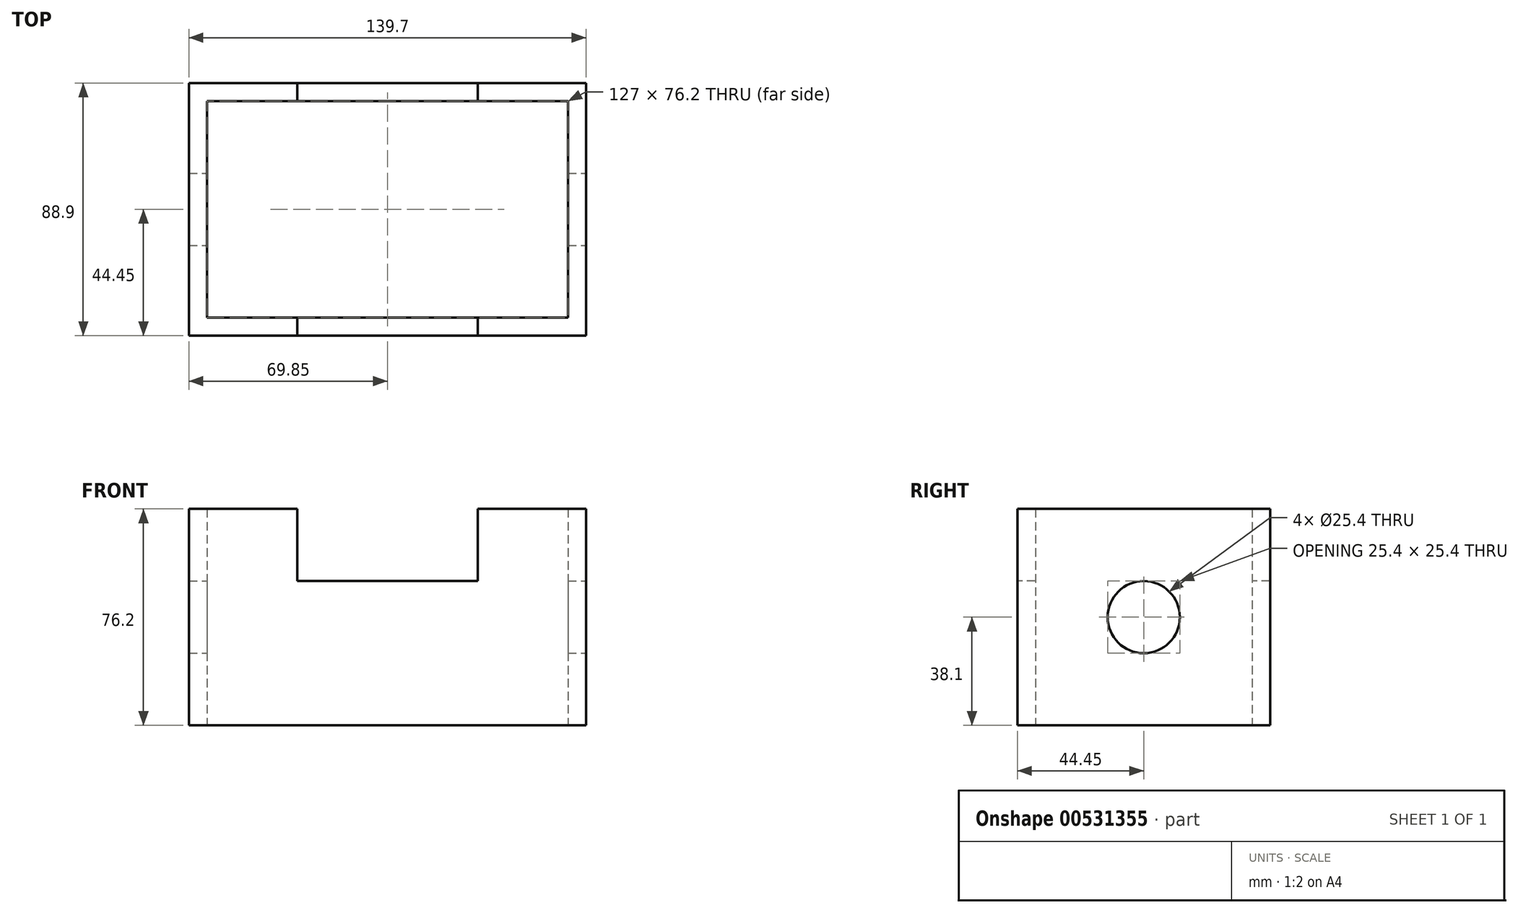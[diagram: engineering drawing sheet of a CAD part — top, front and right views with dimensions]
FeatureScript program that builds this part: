
annotation { "Feature Type Name" : "Feature", "Feature Type Description" : "" }
export const myFeature = defineFeature(function(context is Context, id is Id, definition is map)
    precondition{}
    {
        {
            var Q0;
            Q0=qCreatedBy(makeId("Top.planeOp"),FACE);
            var sketch = newSketch(context, id + "F0", { "sketchPlane" : qUnion([Q0])});
            skLineSegment(sketch, "E0.bottom", {"start": v(63.5, -38.1) * mm, "end": v(-63.5, -38.1) * mm});
            skLineSegment(sketch, "E0.top", {"start": v(63.5, 38.1) * mm, "end": v(-63.5, 38.1) * mm});
            skLineSegment(sketch, "E0.left", {"start": v(63.5, -38.1) * mm, "end": v(63.5, 38.1) * mm});
            skLineSegment(sketch, "E0.right", {"start": v(-63.5, -38.1) * mm, "end": v(-63.5, 38.1) * mm});
            skPoint(sketch, "E0.middle", {"position": v(0, 0) * mm});
            skLineSegment(sketch, "E1.bottom", {"start": v(69.85, -44.45) * mm, "end": v(-69.85, -44.45) * mm});
            skLineSegment(sketch, "E1.top", {"start": v(69.85, 44.45) * mm, "end": v(-69.85, 44.45) * mm});
            skLineSegment(sketch, "E1.left", {"start": v(69.85, -44.45) * mm, "end": v(69.85, 44.45) * mm});
            skLineSegment(sketch, "E1.right", {"start": v(-69.85, -44.45) * mm, "end": v(-69.85, 44.45) * mm});
            skSolve(sketch);
        }
        {
            var Q0;
            Q0=makeQuery(id+"F0.imprint","IMPRINT",FACE,{"disambiguationData":[TD([[makeQuery(id+"F0.imprint","IMPRINT",EDGE,{"derivedFrom":sQuery(id+"F0.wireOp",EDGE,"E0.bottom")}),1.0]])]});
            extrude(context, id + "F1", {"entities" : qUnion([Q0]), "depth" : 76.2 * mm, "offsetDistance" : 25.4 * mm});
        }
        {
            var Q0;
            Q0=makeQuery(id+"F1.opExtrude","SWEPT_FACE",FACE,{"disambiguationData":[OSD([sQuery(id+"F0.wireOp",EDGE,"E1.bottom")])]});
            var sketch = newSketch(context, id + "F2", { "sketchPlane" : qUnion([Q0])});
            skLineSegment(sketch, "E2.bottom", {"start": v(-31.75, 76.2) * mm, "end": v(31.75, 76.2) * mm});
            skLineSegment(sketch, "E2.top", {"start": v(-31.75, 50.8) * mm, "end": v(31.75, 50.8) * mm});
            skLineSegment(sketch, "E2.left", {"start": v(-31.75, 76.2) * mm, "end": v(-31.75, 50.8) * mm});
            skLineSegment(sketch, "E2.right", {"start": v(31.75, 76.2) * mm, "end": v(31.75, 50.8) * mm});
            skSolve(sketch);
        }
        {
            var Q0;
            Q0=makeQuery(id+"F2.imprint","IMPRINT",FACE,{"disambiguationData":[TD([[makeQuery(id+"F2.imprint","IMPRINT",EDGE,{"derivedFrom":sQuery(id+"F2.wireOp",EDGE,"E2.bottom")}),1.0]])]});
            extrude(context, id + "F3", {"entities" : qUnion([Q0]), "operationType" : NewBodyOperationType.REMOVE, "oppositeDirection" : true, "depth" : 166.37 * mm, "offsetDistance" : 25.4 * mm});
        }
        {
            var Q0;
            Q0=makeQuery(id+"F1.opExtrude","SWEPT_FACE",FACE,{"disambiguationData":[OSD([sQuery(id+"F0.wireOp",EDGE,"E1.left")])]});
            var sketch = newSketch(context, id + "F4", { "sketchPlane" : qUnion([Q0])});
            skCircle(sketch, "E3", {"center": v(0, 38.1) * mm, "radius": 12.7 * mm});
            skSolve(sketch);
        }
        {
            var Q0;
            Q0=makeQuery(id+"F4.imprint","IMPRINT",FACE,{"disambiguationData":[TD([[makeQuery(id+"F4.imprint","IMPRINT",EDGE,{"derivedFrom":sQuery(id+"F4.wireOp",EDGE,"E3")}),1.0]])]});
            extrude(context, id + "F5", {"entities" : qUnion([Q0]), "operationType" : NewBodyOperationType.REMOVE, "oppositeDirection" : true, "depth" : 213.36 * mm, "offsetDistance" : 25.4 * mm});
        }
    });
